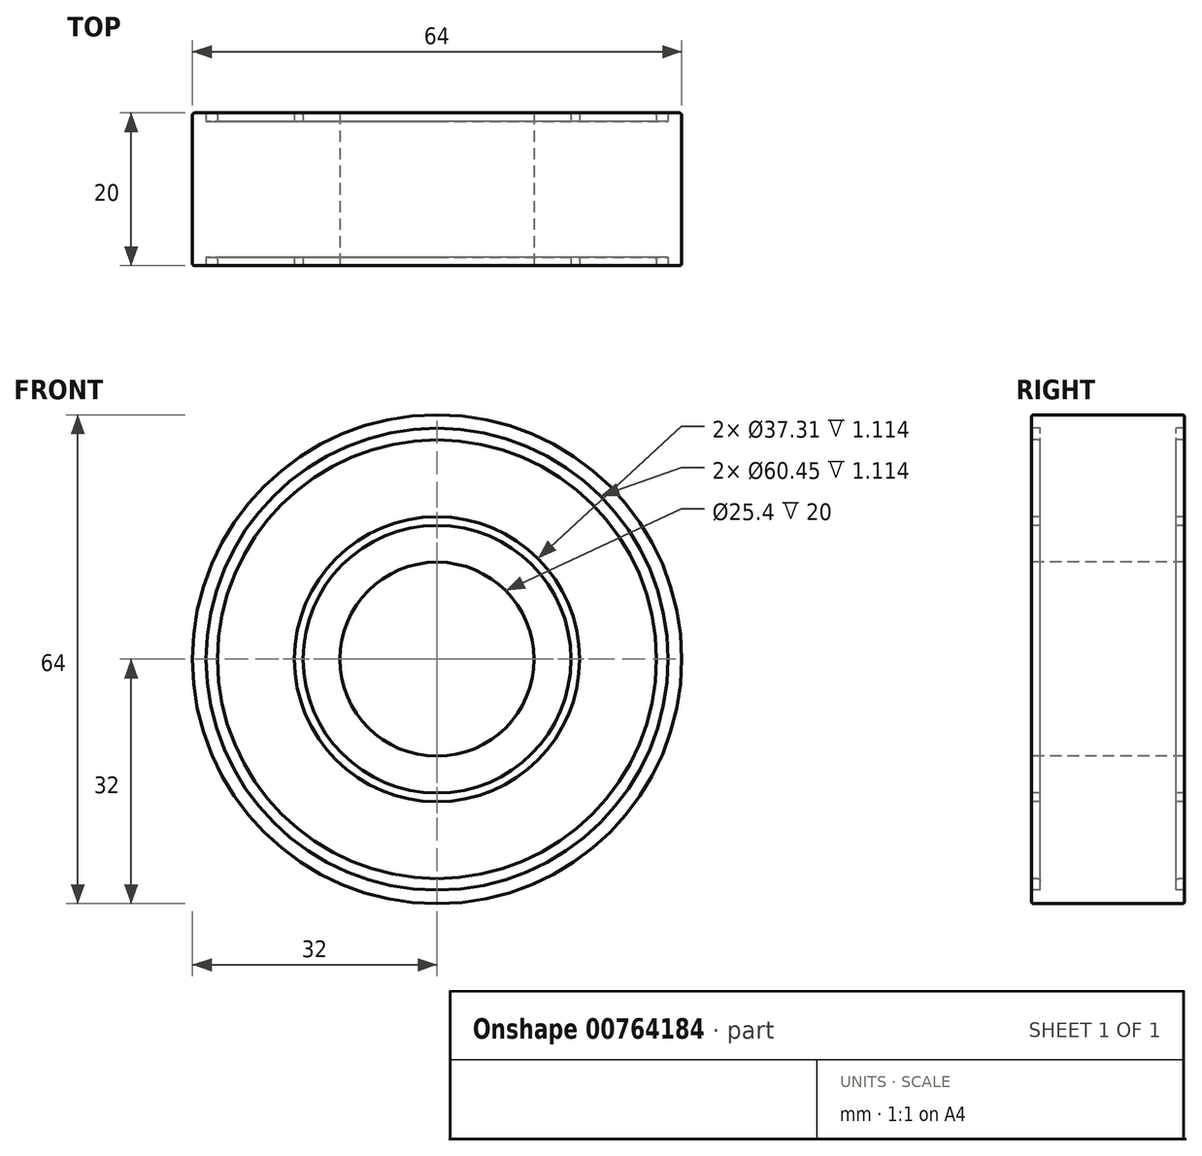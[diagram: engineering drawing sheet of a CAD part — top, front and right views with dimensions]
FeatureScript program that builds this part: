
annotation { "Feature Type Name" : "Feature", "Feature Type Description" : "" }
export const myFeature = defineFeature(function(context is Context, id is Id, definition is map)
    precondition{}
    {
        {
            var Q0;
            Q0=qCreatedBy(makeId("Right.planeOp"),FACE);
            var sketch = newSketch(context, id + "F0", { "sketchPlane" : qUnion([Q0])});
            skLineSegment(sketch, "E0", {"start": v(0, 0) * mm, "end": v(0, 12.7) * mm, "construction": true});
            skLineSegment(sketch, "E1", {"start": v(0, 12.7) * mm, "end": v(-10, 12.7) * mm});
            skLineSegment(sketch, "E2", {"start": v(-10, 12.7) * mm, "end": v(-10, 17.22) * mm});
            skLineSegment(sketch, "E3", {"start": v(-9.7, 17.52) * mm, "end": v(-8.89, 17.52) * mm});
            skLineSegment(sketch, "E4", {"start": v(-8.89, 17.52) * mm, "end": v(-8.89, 18.66) * mm});
            skLineSegment(sketch, "E5", {"start": v(-8.89, 18.66) * mm, "end": v(-10, 18.66) * mm});
            skLineSegment(sketch, "E6", {"start": v(-10, 18.66) * mm, "end": v(-10, 28.4) * mm});
            skLineSegment(sketch, "E7", {"start": v(-9.7, 28.7) * mm, "end": v(-9.19, 28.7) * mm});
            skLineSegment(sketch, "E8", {"start": v(-8.89, 29) * mm, "end": v(-8.89, 30.23) * mm});
            skLineSegment(sketch, "E9", {"start": v(-8.89, 30.23) * mm, "end": v(-10, 30.23) * mm});
            skLineSegment(sketch, "E10", {"start": v(-10, 30.23) * mm, "end": v(-10, 31.7) * mm});
            skLineSegment(sketch, "E11", {"start": v(-9.7, 32) * mm, "end": v(0, 32) * mm});
            skPoint(sketch, "E12.visualSharp", {"position": v(-8.89, 28.7) * mm});
            skArc(sketch, "E12.filletArc", {"start": v(-9.19, 28.7) * mm, "mid": v(-8.97, 28.8) * mm, "end": v(-8.89, 29) * mm});
            skPoint(sketch, "E13.visualSharp", {"position": v(-10, 28.7) * mm});
            skArc(sketch, "E13.filletArc", {"start": v(-9.7, 28.7) * mm, "mid": v(-9.91, 28.62) * mm, "end": v(-10, 28.4) * mm});
            skPoint(sketch, "E14.visualSharp", {"position": v(-10, 17.52) * mm});
            skArc(sketch, "E14.filletArc", {"start": v(-9.7, 17.52) * mm, "mid": v(-9.91, 17.43) * mm, "end": v(-10, 17.22) * mm});
            skPoint(sketch, "E15.visualSharp", {"position": v(-10, 32) * mm});
            skArc(sketch, "E15.filletArc", {"start": v(-9.7, 32) * mm, "mid": v(-9.91, 31.91) * mm, "end": v(-10, 31.7) * mm});
            skLineSegment(sketch, "E16.MirrorCS", {"start": v(9.7, 32) * mm, "end": v(0, 32) * mm});
            skLineSegment(sketch, "E17.MirrorCS", {"start": v(10, 30.23) * mm, "end": v(10, 31.7) * mm});
            skArc(sketch, "E18.MirrorCS", {"start": v(9.7, 32) * mm, "mid": v(9.91, 31.91) * mm, "end": v(10, 31.7) * mm});
            skLineSegment(sketch, "E19.MirrorCS", {"start": v(8.89, 30.23) * mm, "end": v(10, 30.23) * mm});
            skLineSegment(sketch, "E20.MirrorCS", {"start": v(8.89, 29) * mm, "end": v(8.89, 30.23) * mm});
            skArc(sketch, "E21.MirrorCS", {"start": v(9.19, 28.7) * mm, "mid": v(8.97, 28.8) * mm, "end": v(8.89, 29) * mm});
            skLineSegment(sketch, "E22.MirrorCS", {"start": v(9.7, 28.7) * mm, "end": v(9.19, 28.7) * mm});
            skArc(sketch, "E23.MirrorCS", {"start": v(9.7, 28.7) * mm, "mid": v(9.91, 28.62) * mm, "end": v(10, 28.4) * mm});
            skLineSegment(sketch, "E24.MirrorCS", {"start": v(10, 18.66) * mm, "end": v(10, 28.4) * mm});
            skLineSegment(sketch, "E25.MirrorCS", {"start": v(8.89, 18.66) * mm, "end": v(10, 18.66) * mm});
            skLineSegment(sketch, "E26.MirrorCS", {"start": v(8.89, 17.52) * mm, "end": v(8.89, 18.66) * mm});
            skLineSegment(sketch, "E27.MirrorCS", {"start": v(9.7, 17.52) * mm, "end": v(8.89, 17.52) * mm});
            skArc(sketch, "E28.MirrorCS", {"start": v(9.7, 17.52) * mm, "mid": v(9.91, 17.43) * mm, "end": v(10, 17.22) * mm});
            skLineSegment(sketch, "E29.MirrorCS", {"start": v(10, 12.7) * mm, "end": v(10, 17.22) * mm});
            skLineSegment(sketch, "E30.MirrorCS", {"start": v(0, 12.7) * mm, "end": v(10, 12.7) * mm});
            skSolve(sketch);
        }
        {
            var Q0;
            Q0=qCreatedBy(makeId("Top.planeOp"),FACE);
            var sketch = newSketch(context, id + "F1", { "sketchPlane" : qUnion([Q0])});
            skLineSegment(sketch, "E31", {"start": v(0, -17.64) * mm, "end": v(0, 14.02) * mm, "construction": true});
            skSolve(sketch);
        }
        {
            var Q0;
            Q0=qSketchRegion(id+"F0",true);
            var Q1;
            Q1=sQuery(id+"F1.wireOp",EDGE,"E31");
            revolve(context, id + "F2", {"surfaceOperationType" : NewSurfaceOperationType.NEW, "entities" : qUnion([Q0]), "axis" : qUnion([Q1]), "revolveType" : RevolveType.FULL});
        }
    });
